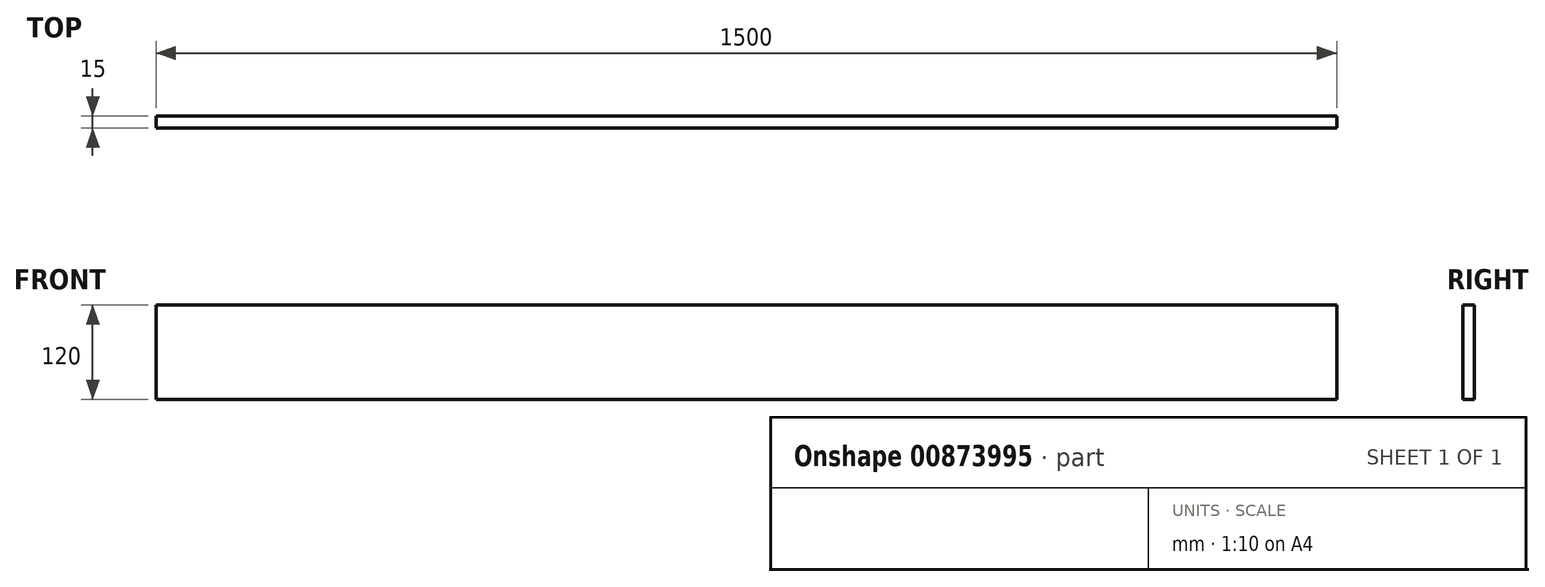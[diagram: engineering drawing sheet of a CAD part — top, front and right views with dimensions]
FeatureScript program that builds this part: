
annotation { "Feature Type Name" : "Feature", "Feature Type Description" : "" }
export const myFeature = defineFeature(function(context is Context, id is Id, definition is map)
    precondition{}
    {
        {
            var Q0;
            Q0=qCreatedBy(makeId("Front.planeOp"),FACE);
            var sketch = newSketch(context, id + "F0", { "sketchPlane" : qUnion([Q0])});
            skLineSegment(sketch, "E0.bottom", {"start": v(0, 0) * mm, "end": v(1500, 0) * mm});
            skLineSegment(sketch, "E0.top", {"start": v(0, 120) * mm, "end": v(1500, 120) * mm});
            skLineSegment(sketch, "E0.left", {"start": v(0, 0) * mm, "end": v(0, 120) * mm});
            skLineSegment(sketch, "E0.right", {"start": v(1500, 0) * mm, "end": v(1500, 120) * mm});
            skSolve(sketch);
        }
        {
            var Q0;
            Q0 = qSketchRegion(id + "F0", true);
            extrude(context, id + "F1", {"entities" : qUnion([Q0]), "depth" : 15 * mm, "offsetDistance" : 25 * mm});
        }
    });
